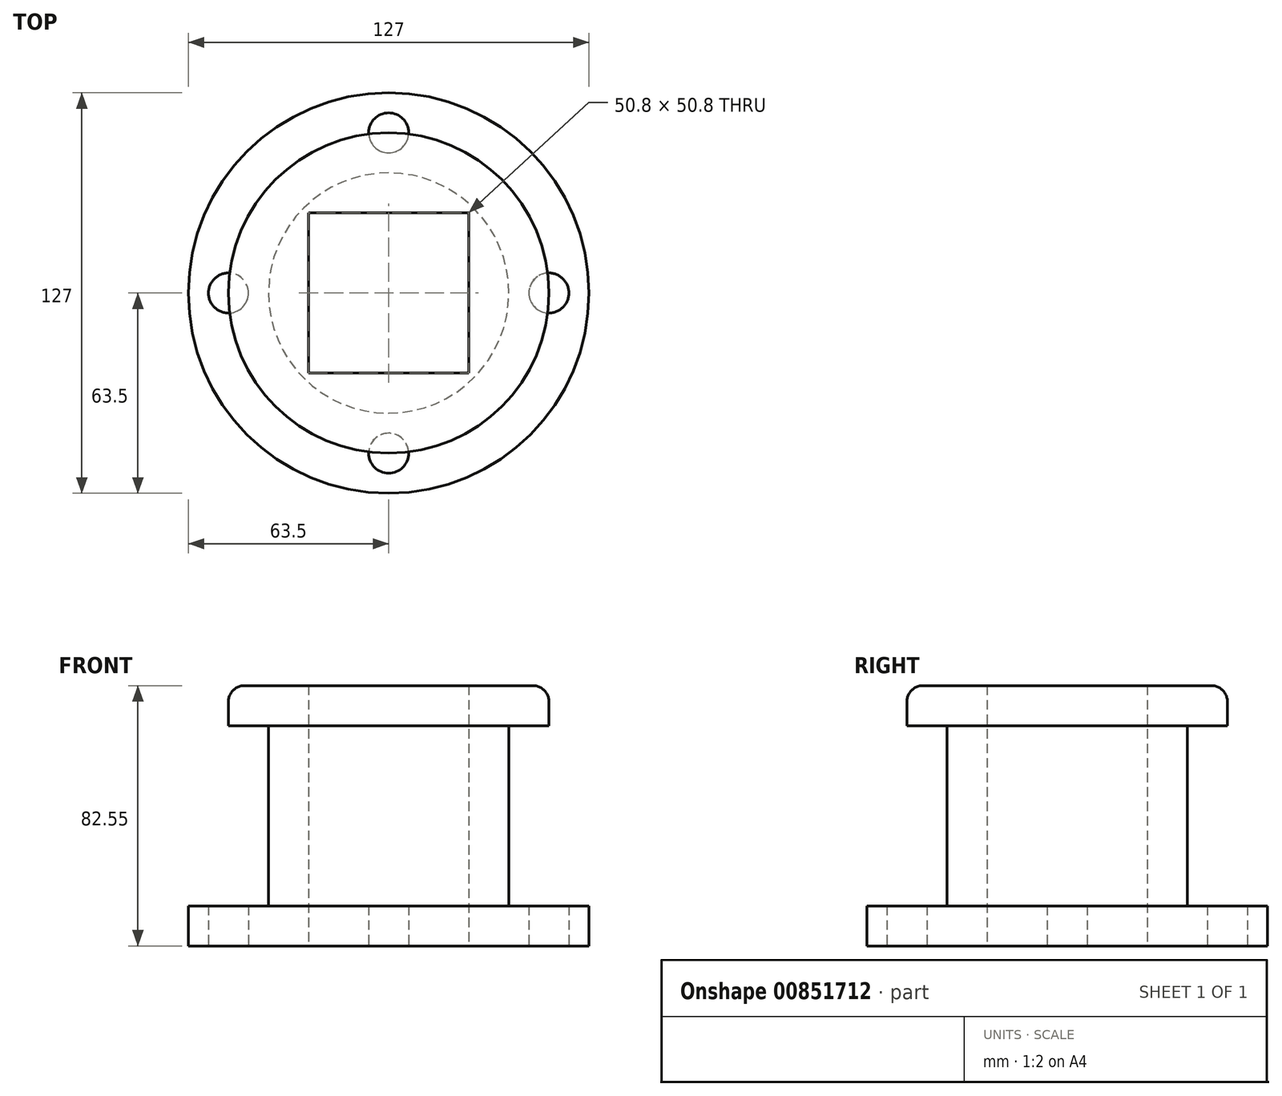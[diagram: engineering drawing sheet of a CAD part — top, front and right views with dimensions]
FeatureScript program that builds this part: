
annotation { "Feature Type Name" : "Feature", "Feature Type Description" : "" }
export const myFeature = defineFeature(function(context is Context, id is Id, definition is map)
    precondition{}
    {
        {
            var Q0;
            Q0=qCreatedBy(makeId("Top.planeOp"),FACE);
            var sketch = newSketch(context, id + "F0", { "sketchPlane" : qUnion([Q0])});
            skCircle(sketch, "E0", {"center": v(0, 0) * mm, "radius": 63.5 * mm});
            skSolve(sketch);
        }
        {
            var Q0;
            Q0 = qSketchRegion(id + "F0", true);
            extrude(context, id + "F1", {"entities" : qUnion([Q0]), "depth" : 12.7 * mm, "offsetDistance" : 25.4 * mm});
        }
        {
            var Q0;
            Q0=makeQuery(id+"F1.opExtrude","CAP_FACE",FACE,{"disambiguationData":[OSD([sQuery(id+"F0.wireOp",EDGE,"E0")])],"isStart":false});
            var sketch = newSketch(context, id + "F2", { "sketchPlane" : qUnion([Q0])});
            skCircle(sketch, "E1", {"center": v(0, 0) * mm, "radius": 38.1 * mm});
            skSolve(sketch);
        }
        {
            var Q0;
            Q0 = qSketchRegion(id + "F2", true);
            extrude(context, id + "F3", {"entities" : qUnion([Q0]), "operationType" : NewBodyOperationType.ADD, "depth" : 57.15 * mm, "offsetDistance" : 25.4 * mm});
        }
        {
            var Q0;
            Q0=makeQuery(id+"F3.opExtrude","CAP_FACE",FACE,{"disambiguationData":[OSD([sQuery(id+"F2.wireOp",EDGE,"E1")])],"isStart":false});
            var sketch = newSketch(context, id + "F4", { "sketchPlane" : qUnion([Q0])});
            skCircle(sketch, "E2", {"center": v(0, 0) * mm, "radius": 50.8 * mm});
            skSolve(sketch);
        }
        {
            var Q0;
            Q0 = qSketchRegion(id + "F4", true);
            extrude(context, id + "F5", {"entities" : qUnion([Q0]), "operationType" : NewBodyOperationType.ADD, "depth" : 12.7 * mm, "offsetDistance" : 25.4 * mm});
        }
        {
            var Q0;
            Q0=makeQuery(id+"F1.opExtrude","CAP_FACE",FACE,{"disambiguationData":[OSD([sQuery(id+"F0.wireOp",EDGE,"E0")])],"isStart":true});
            var sketch = newSketch(context, id + "F6", { "sketchPlane" : qUnion([Q0])});
            skLineSegment(sketch, "E3.top", {"start": v(0, 25.4) * mm, "end": v(25.4, 25.4) * mm});
            skLineSegment(sketch, "E3.right", {"start": v(25.4, 0) * mm, "end": v(25.4, 25.4) * mm});
            skLineSegment(sketch, "E4.top", {"start": v(0, -25.4) * mm, "end": v(25.4, -25.4) * mm});
            skLineSegment(sketch, "E4.right", {"start": v(25.4, 0) * mm, "end": v(25.4, -25.4) * mm});
            skLineSegment(sketch, "E5.top", {"start": v(0, -25.4) * mm, "end": v(-25.4, -25.4) * mm});
            skLineSegment(sketch, "E5.right", {"start": v(-25.4, 0) * mm, "end": v(-25.4, -25.4) * mm});
            skLineSegment(sketch, "E6.top", {"start": v(0, 25.4) * mm, "end": v(-25.4, 25.4) * mm});
            skLineSegment(sketch, "E6.right", {"start": v(-25.4, 0) * mm, "end": v(-25.4, 25.4) * mm});
            skSolve(sketch);
        }
        {
            var Q0;
            Q0=makeQuery(id+"F6.imprint","IMPRINT",FACE,{"disambiguationData":[TD([[makeQuery(id+"F6.imprint","IMPRINT",EDGE,{"derivedFrom":sQuery(id+"F6.wireOp",EDGE,"E3.top")}),1.0]])]});
            var sketch = newSketch(context, id + "F7", { "sketchPlane" : qUnion([Q0])});
            skCircle(sketch, "E7", {"center": v(0, 50.8) * mm, "radius": 6.35 * mm});
            skCircle(sketch, "E8", {"center": v(50.8, 0) * mm, "radius": 6.35 * mm});
            skCircle(sketch, "E9", {"center": v(0, -50.8) * mm, "radius": 6.35 * mm});
            skCircle(sketch, "E10", {"center": v(-50.8, 0) * mm, "radius": 6.35 * mm});
            skSolve(sketch);
        }
        {
            var Q0;
            Q0 = qSketchRegion(id + "F7", true);
            extrude(context, id + "F8", {"entities" : qUnion([Q0]), "operationType" : NewBodyOperationType.REMOVE, "oppositeDirection" : true, "depth" : 25.4 * mm, "offsetDistance" : 25.4 * mm});
        }
        {
            var Q0;
            Q0 = qSketchRegion(id + "F6", true);
            extrude(context, id + "F9", {"entities" : qUnion([Q0]), "operationType" : NewBodyOperationType.REMOVE, "oppositeDirection" : true, "depth" : 127 * mm, "offsetDistance" : 25.4 * mm});
        }
        {
            var Q0;
            Q0=makeQuery(id+"F5.opExtrude","CAP_EDGE",EDGE,{"disambiguationData":[OSD([sQuery(id+"F4.wireOp",EDGE,"E2")])],"isStart":false});
            fillet(context, id + "F10", {"entities" : qUnion([Q0]), "radius" : 5.08 * mm, "tangentPropagation" : true, "allowEdgeOverflow" : false});
        }
    });
